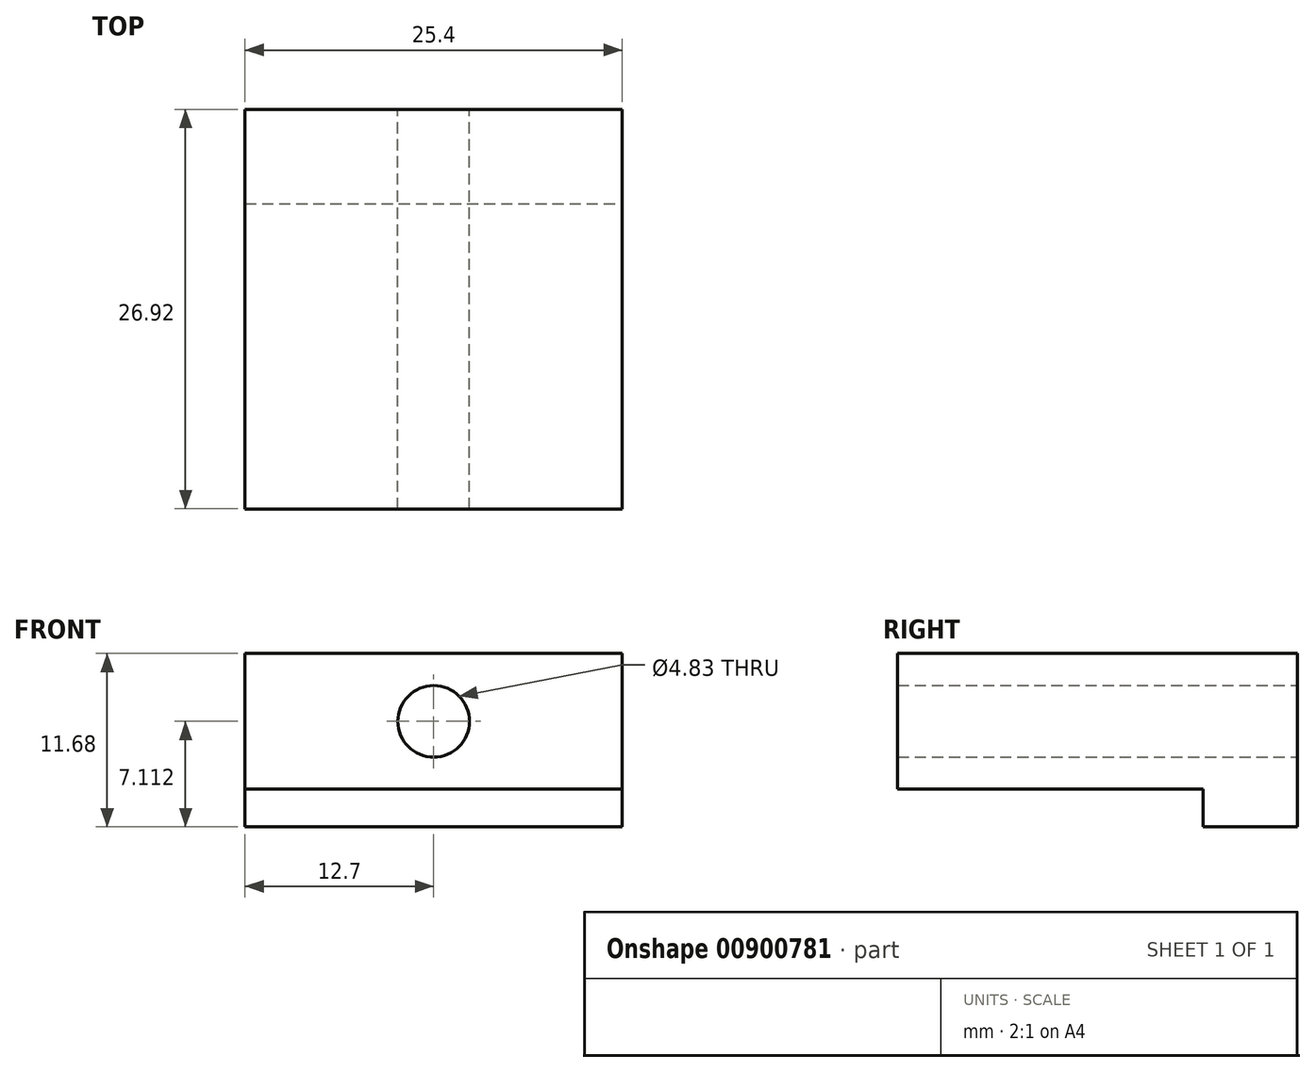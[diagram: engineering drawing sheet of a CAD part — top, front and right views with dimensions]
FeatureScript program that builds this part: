
annotation { "Feature Type Name" : "Feature", "Feature Type Description" : "" }
export const myFeature = defineFeature(function(context is Context, id is Id, definition is map)
    precondition{}
    {
        {
            var Q0;
            Q0=qCreatedBy(makeId("Front.planeOp"),FACE);
            var sketch = newSketch(context, id + "F0", { "sketchPlane" : qUnion([Q0])});
            skLineSegment(sketch, "E0.bottom", {"start": v(0, 0) * mm, "end": v(25.4, 0) * mm});
            skLineSegment(sketch, "E0.top", {"start": v(0, 11.68) * mm, "end": v(25.4, 11.68) * mm});
            skLineSegment(sketch, "E0.left", {"start": v(0, 0) * mm, "end": v(0, 11.68) * mm});
            skLineSegment(sketch, "E0.right", {"start": v(25.4, 0) * mm, "end": v(25.4, 11.68) * mm});
            skCircle(sketch, "E1", {"center": v(12.7, 7.11) * mm, "radius": 2.41 * mm});
            skSolve(sketch);
        }
        {
            var Q0;
            Q0=makeQuery(id+"F0.imprint","IMPRINT",FACE,{"disambiguationData":[TD([[makeQuery(id+"F0.imprint","IMPRINT",EDGE,{"derivedFrom":sQuery(id+"F0.wireOp",EDGE,"E0.bottom")}),1.0]])]});
            extrude(context, id + "F1", {"entities" : qUnion([Q0]), "depth" : 26.92 * mm, "offsetDistance" : 25.4 * mm});
        }
        {
            var Q0;
            Q0=makeQuery(id+"F1.opExtrude","SWEPT_FACE",FACE,{"disambiguationData":[OSD([sQuery(id+"F0.wireOp",EDGE,"E0.right")])]});
            var sketch = newSketch(context, id + "F2", { "sketchPlane" : qUnion([Q0])});
            skLineSegment(sketch, "E2.bottom", {"start": v(-30.48, 2.54) * mm, "end": v(-6.35, 2.54) * mm});
            skLineSegment(sketch, "E2.top", {"start": v(-30.48, -16.56) * mm, "end": v(-6.35, -16.56) * mm});
            skLineSegment(sketch, "E2.left", {"start": v(-30.48, 2.54) * mm, "end": v(-30.48, -16.56) * mm});
            skLineSegment(sketch, "E2.right", {"start": v(-6.35, 2.54) * mm, "end": v(-6.35, -16.56) * mm});
            skSolve(sketch);
        }
        {
            var Q0;
            {var subQ0=sQuery(id+"F2.wireOp",EDGE,"E2.right");var subQ1=sQuery(id+"F2.wireOp",EDGE,"E2.bottom");var subQ2=makeQuery(id+"F2.imprint","INTERSECT",VERTEX,{"derivedFrom":[subQ1,subQ0]});Q0=makeQuery(id+"F2.imprint","IMPRINT",FACE,{"disambiguationData":[TD([[makeQuery(id+"F2.imprint","IMPRINT",EDGE,{"disambiguationData":[TD([[subQ2,1.0]])],"derivedFrom":subQ1}),-1.0]])]});}
            extrude(context, id + "F3", {"entities" : qUnion([Q0]), "operationType" : NewBodyOperationType.REMOVE, "endBound" : BoundingType.THROUGH_ALL, "oppositeDirection" : true, "depth" : 25.4 * mm, "offsetDistance" : 25.4 * mm});
        }
    });
